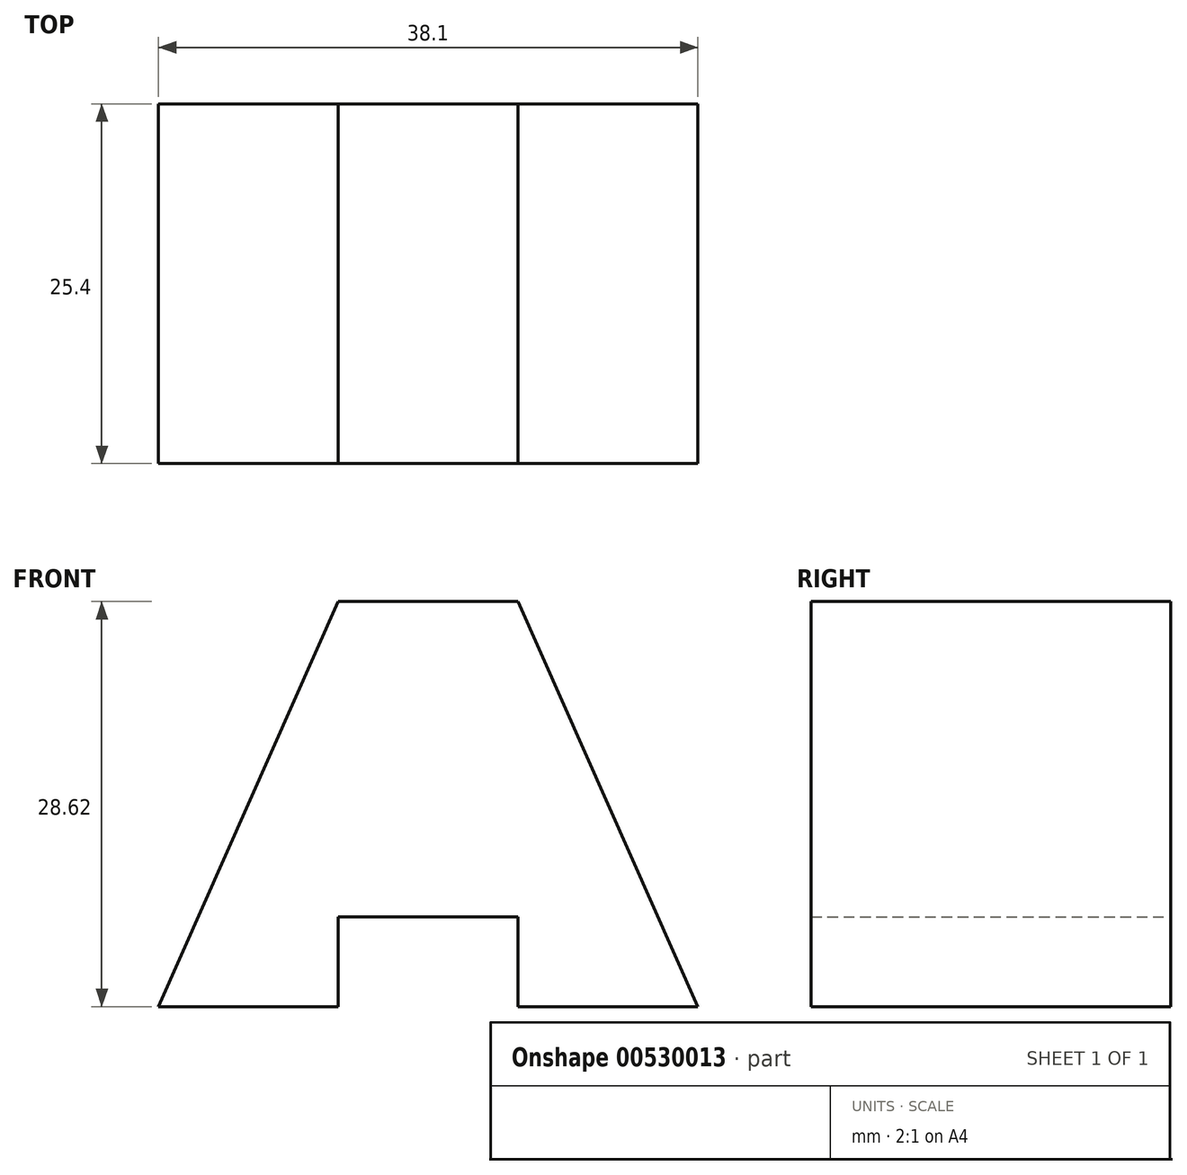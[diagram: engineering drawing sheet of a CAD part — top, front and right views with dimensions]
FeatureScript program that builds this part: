
annotation { "Feature Type Name" : "Feature", "Feature Type Description" : "" }
export const myFeature = defineFeature(function(context is Context, id is Id, definition is map)
    precondition{}
    {
        {
            var Q0;
            Q0=qCreatedBy(makeId("Front.planeOp"),FACE);
            var sketch = newSketch(context, id + "F0", { "sketchPlane" : qUnion([Q0])});
            skLineSegment(sketch, "E0", {"start": v(-53.78, 51.04) * mm, "end": v(-66.48, 22.42) * mm});
            skLineSegment(sketch, "E1", {"start": v(-53.78, 51.04) * mm, "end": v(-41.08, 51.04) * mm});
            skLineSegment(sketch, "E2", {"start": v(-41.08, 51.04) * mm, "end": v(-28.38, 22.42) * mm});
            skLineSegment(sketch, "E3", {"start": v(-66.48, 22.42) * mm, "end": v(-53.78, 22.42) * mm});
            skLineSegment(sketch, "E4", {"start": v(-53.78, 22.42) * mm, "end": v(-53.78, 28.77) * mm});
            skLineSegment(sketch, "E5", {"start": v(-53.78, 28.77) * mm, "end": v(-41.08, 28.77) * mm});
            skLineSegment(sketch, "E6", {"start": v(-41.08, 28.77) * mm, "end": v(-41.08, 22.42) * mm});
            skLineSegment(sketch, "E7", {"start": v(-41.08, 22.42) * mm, "end": v(-28.38, 22.42) * mm});
            skSolve(sketch);
        }
        {
            var Q0;
            Q0=makeQuery(id+"F0.imprint","IMPRINT",FACE,{"disambiguationData":[TD([[makeQuery(id+"F0.imprint","IMPRINT",EDGE,{"derivedFrom":sQuery(id+"F0.wireOp",EDGE,"E0")}),1.0]])]});
            extrude(context, id + "F1", {"entities" : qUnion([Q0]), "depth" : 25.4 * mm, "offsetDistance" : 25.4 * mm});
        }
    });
